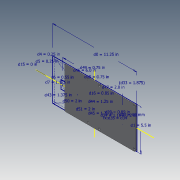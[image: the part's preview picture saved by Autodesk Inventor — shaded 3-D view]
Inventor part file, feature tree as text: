
AUTODESK INVENTOR PART (.ipt)
format: ipt  version: 2020.3 (Build 243373000, 373)  size: 161,280 bytes
history: native  units: in
note: dims shown in document units (in); Inventor stores cm internally (conversion verified against a paired STEP export)
features: sketch x2, extrude x2, hole x2, fillet x2
ambient origin geometry x8: Origin, YZ Plane, XZ Plane, XY Plane, X Axis, Y Axis, Z Axis, Center Point
bodies: Solid1 (feature_tree)
feature tree (8):
  sketch  "Sketch1"  dims[d0=11.25in d1=5.5in]
  extrude  "Extrusion1"  Depth=5.5in
  hole  "Hole1"  [1 undecoded]
  fillet  "Fillet1"  Radius=0.55in
  hole  "Hole2"  [1 undecoded]
  extrude  "Extrusion2"  TaperAngle=0.0deg  [1 undecoded]
  fillet  "Fillet2"  Radius=0.85in
  sketch  "Sketch2"  dims[d4=0.25in d5=0.25in d6=0.55in d7=1.125in d15=0.0in d16=0.85in d20=0.89in d22=2.3622in d23=0.125in d24=0.0in d25=0.24in d26=0.75in d27=0.375in d28=0.25in d29=0.5635in d30=1.0in d31=0.8108in d32=0.25in d33=1.875in d34=0.58in d35=0.58in d36=0.123in d37=0.75in d38=0.375in d39=0.25in d40=0.5635in d41=1.0in d42=0.8108in d43=1.375in d44=1.25in d45=1.25in d46=6.0in d47=2.0in d48=0.75in d49=0.75in d50=2.0in d51=2.0in d52=0.0in d53=1.75in d54=6.0in d55=1.0in d56=0.0in d57=0.125in]
note: 3 required parameter values undecoded (feature->parameter linkage not recoverable at this tier; creation-order binding heuristic only, values carry confidence <= 0.55)
